# Revit family: Haworth_Epure_Pedestal_DeskHeightIndependent_EU_PRELIMINARY
name_source: partatom
category: Furniture
units: mm (PartAtom-declared; Revit-internal decimal feet)

## family parameters
Always vertical = Yes
Cut with Voids When Loaded = No
OmniClass Number = 23.40.70.14.64.11
OmniClass Title = Office Furniture
Room Calculation Point = No
Shared = No
Work Plane-Based = No

## types (2) — shared parameters
Actual Depth = 80 cm
Actual Height = 73 cm
Actual Width = 44 cm
Assembly Code = E2020200
Description = Haworth - Epure - Desk Height Independent Pedestal
Filing Drawer = 13cm = Yes
Filing Drawer = 19cm = No
Filing Drawer Large = 18 cm
Filing Drawer Medium = 12 cm
Filing Drawer Small = 13 cm
Glide Finish = Haworth _ Polymer _ Black
Handle 1 = No
Manufacturer = Haworth
Model = EUHP08F3XX
Pen Drawer = 5 cm
Revision Number = 1
Rounded Top = No
Simple Drawer = 32 cm
Simple Drawer = 32cm = Yes
Size = Verify Final Dim.w/ Haworth
Squared Top = Yes
URL = https://www.haworth.com
URL - Product = https://www.haworth.com
Warranty = http://www.haworth.com
with Pull = Yes
without Pull = No

## per-type parameters (varying)
| type | Filing Drawer = 12cm | Filing Drawer = 16cm | Handle 2 | Metal Handle | Pen Drawer = 5cm | Trim Finish |
| 3 Drawers without Pen Tray | No | Yes | Yes | No | No | Haworth _ Polymer _ Undecided |
| 3 Drawers with Pen Tray | Yes | No | No | Yes | Yes | Haworth _ Paint _ Smooth Plaster |

## geometry (parser evidence)
native form markers: Sweep x4
no freeform markers — native parametric forms only
